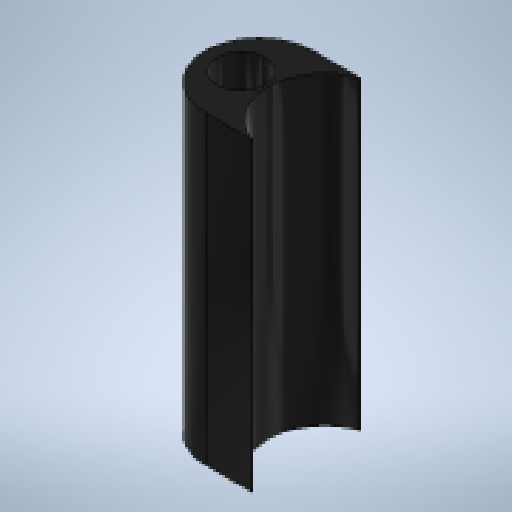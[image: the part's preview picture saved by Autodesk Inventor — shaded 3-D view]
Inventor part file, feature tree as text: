
AUTODESK INVENTOR PART (.ipt)
format: ipt  version: 2024 (Build 280153000, 153)  size: 271,872 bytes
history: native  units: mm
features: extrude x1, sketch x1
ambient origin geometry x8: Origin, YZ Plane, XZ Plane, XY Plane, X Axis, Y Axis, Z Axis, Center Point
bodies: Body1 (feature_tree)
feature tree (2):
  extrude  "Extrusion2"  [1 undecoded]
  sketch  "Skizze1"  dims[d2=53.0mm d3=0.0mm]
note: 1 required parameter value undecoded (feature->parameter linkage not recoverable at this tier; creation-order binding heuristic only, values carry confidence <= 0.55)
